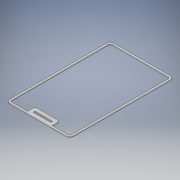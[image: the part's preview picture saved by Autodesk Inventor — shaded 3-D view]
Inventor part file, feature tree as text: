
AUTODESK INVENTOR PART (.ipt)
format: ipt  version: 2018 (Build 220112000, 112)  size: 179,712 bytes
history: native  units: mm
features: other x5, sketch x3, projected_geometry x2
ambient origin geometry x8: Origin, YZ Plane, XZ Plane, XY Plane, X Axis, Y Axis, Z Axis, Center Point
bodies: Volumenkörper1 (feature_tree)
feature tree (10):
  other  "Fläche1"
  other  "Eckenrundung1"
  sketch  "Skizze1"  dims[d0=162.0mm]
  other  "Grobblech1"
  sketch  "Skizze2"  dims[d1=265.0mm]
  projected_geometry  "Projizierte Kontur1"
  sketch  "Skizze5"  dims[d2=2.0mm d3=10.0mm d4=5.0mm d7=45.0mm d8=5.0mm d10=9.0mm d17=2.0mm d18=0.0mm d37=5.0mm d38=9.0mm d39=2.0mm d40=0.0mm d41=5.0mm d44=45.0deg d45=4.0mm d70=10.0mm d71=60.0mm]
  projected_geometry  "Projizierte Kontur3"
  other  "Ausklinkung1"
  other  "Ausklinkung2"
